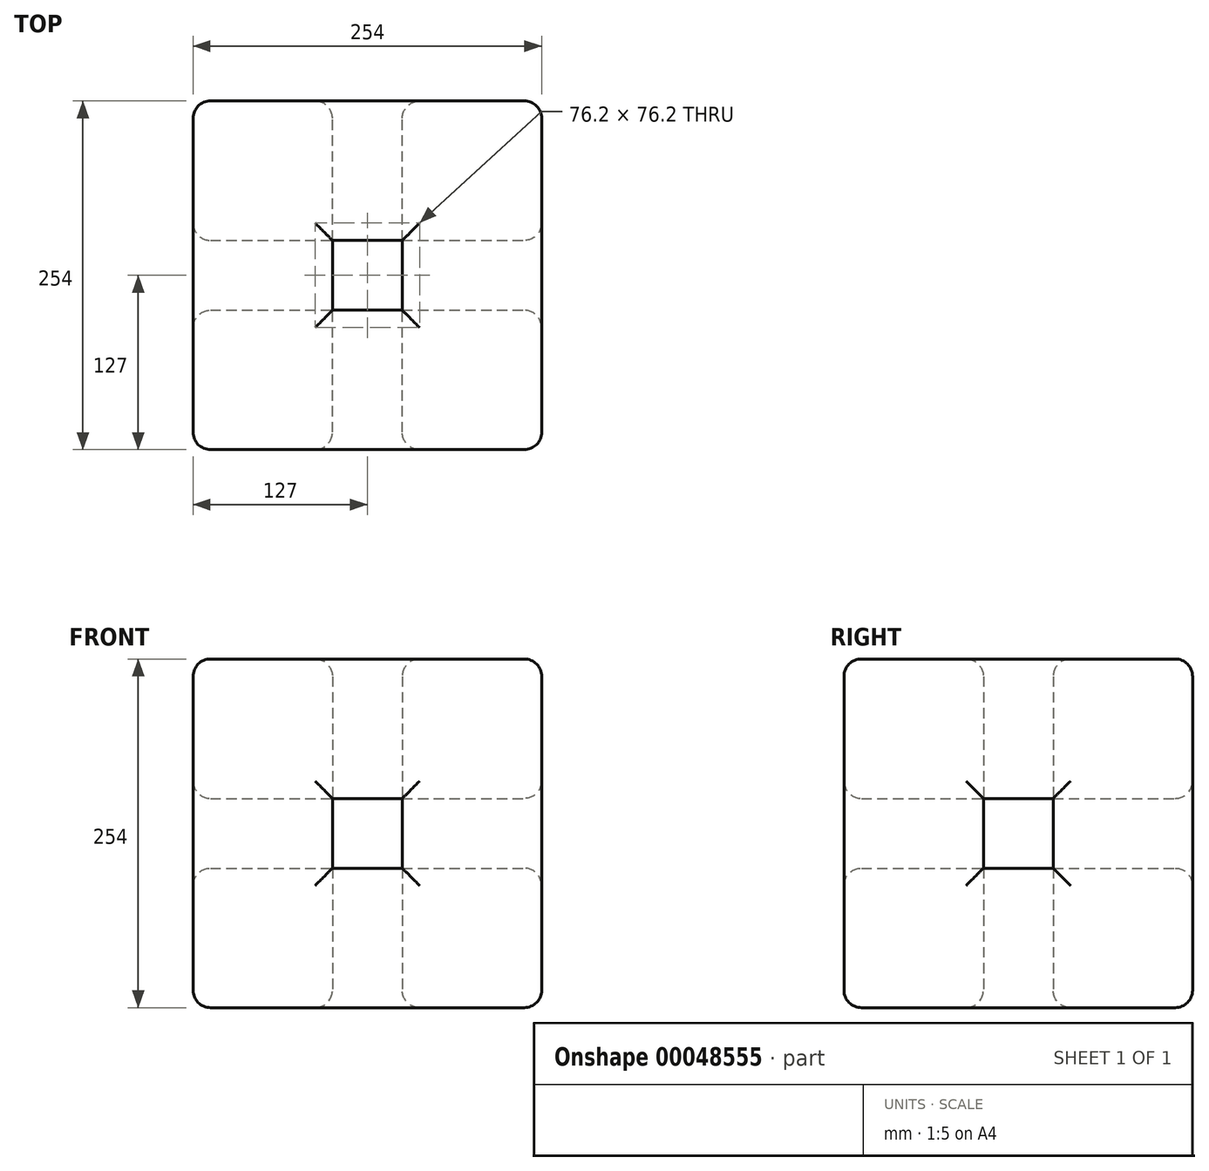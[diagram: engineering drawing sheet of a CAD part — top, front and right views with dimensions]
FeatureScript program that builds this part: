
annotation { "Feature Type Name" : "Feature", "Feature Type Description" : "" }
export const myFeature = defineFeature(function(context is Context, id is Id, definition is map)
    precondition{}
    {
        {
            var Q0;
            Q0=qCreatedBy(makeId("Front.planeOp"),FACE);
            var sketch = newSketch(context, id + "F0", { "sketchPlane" : qUnion([Q0])});
            skLineSegment(sketch, "E0.rect.bottom", {"start": v(127, 127) * mm, "end": v(-127, 127) * mm});
            skLineSegment(sketch, "E0.rect.top", {"start": v(127, -127) * mm, "end": v(-127, -127) * mm});
            skLineSegment(sketch, "E0.rect.left", {"start": v(127, 127) * mm, "end": v(127, -127) * mm});
            skLineSegment(sketch, "E0.rect.right", {"start": v(-127, 127) * mm, "end": v(-127, -127) * mm});
            skPoint(sketch, "E0.rect.middle", {"position": v(0, 0) * mm});
            skSolve(sketch);
        }
        {
            var Q0;
            Q0 = qSketchRegion(id + "F0", true);
            extrude(context, id + "F6", {"entities" : qUnion([Q0]), "endBound" : BoundingType.SYMMETRIC, "depth" : 254 * mm});
        }
        {
            var Q0;
            Q0=makeQuery(id+"F6.opExtrude","SWEPT_FACE",FACE,{"disambiguationData":[OSD([sQuery(id+"F0.wireOp",EDGE,"E0.rect.top")])]});
            var sketch = newSketch(context, id + "F7", { "sketchPlane" : qUnion([Q0])});
            skLineSegment(sketch, "E1.rect.bottom", {"start": v(25.4, 25.4) * mm, "end": v(-25.4, 25.4) * mm});
            skLineSegment(sketch, "E1.rect.top", {"start": v(25.4, -25.4) * mm, "end": v(-25.4, -25.4) * mm});
            skLineSegment(sketch, "E1.rect.left", {"start": v(25.4, 25.4) * mm, "end": v(25.4, -25.4) * mm});
            skLineSegment(sketch, "E1.rect.right", {"start": v(-25.4, 25.4) * mm, "end": v(-25.4, -25.4) * mm});
            skPoint(sketch, "E1.rect.middle", {"position": v(0, 0) * mm});
            skSolve(sketch);
        }
        {
            var Q0;
            Q0 = qSketchRegion(id + "F7", true);
            extrude(context, id + "F1", {"entities" : qUnion([Q0]), "operationType" : NewBodyOperationType.REMOVE, "endBound" : BoundingType.THROUGH_ALL, "oppositeDirection" : true, "depth" : 25.4 * mm});
        }
        {
            var Q0;
            Q0=makeQuery(id+"F6.opExtrude","SWEPT_FACE",FACE,{"disambiguationData":[OSD([sQuery(id+"F0.wireOp",EDGE,"E0.rect.left")])]});
            var sketch = newSketch(context, id + "F2", { "sketchPlane" : qUnion([Q0])});
            skLineSegment(sketch, "E2.rect.bottom", {"start": v(25.4, 25.4) * mm, "end": v(-25.4, 25.4) * mm});
            skLineSegment(sketch, "E2.rect.top", {"start": v(25.4, -25.4) * mm, "end": v(-25.4, -25.4) * mm});
            skLineSegment(sketch, "E2.rect.left", {"start": v(25.4, 25.4) * mm, "end": v(25.4, -25.4) * mm});
            skLineSegment(sketch, "E2.rect.right", {"start": v(-25.4, 25.4) * mm, "end": v(-25.4, -25.4) * mm});
            skPoint(sketch, "E2.rect.middle", {"position": v(0, 0) * mm});
            skSolve(sketch);
        }
        {
            var Q0;
            Q0 = qSketchRegion(id + "F2", true);
            extrude(context, id + "F3", {"entities" : qUnion([Q0]), "operationType" : NewBodyOperationType.REMOVE, "endBound" : BoundingType.THROUGH_ALL, "oppositeDirection" : true, "depth" : 25.4 * mm});
        }
        {
            var Q0;
            Q0=makeQuery(id+"F6.opExtrude","CAP_FACE",FACE,{"disambiguationData":[OSD([sQuery(id+"F0.wireOp",EDGE,"E0.rect.bottom"),sQuery(id+"F0.wireOp",EDGE,"E0.rect.top"),sQuery(id+"F0.wireOp",EDGE,"E0.rect.left"),sQuery(id+"F0.wireOp",EDGE,"E0.rect.right")])],"isStart":true});
            var sketch = newSketch(context, id + "F4", { "sketchPlane" : qUnion([Q0])});
            skLineSegment(sketch, "E3.rect.bottom", {"start": v(25.4, 25.4) * mm, "end": v(-25.4, 25.4) * mm});
            skLineSegment(sketch, "E3.rect.top", {"start": v(25.4, -25.4) * mm, "end": v(-25.4, -25.4) * mm});
            skLineSegment(sketch, "E3.rect.left", {"start": v(25.4, 25.4) * mm, "end": v(25.4, -25.4) * mm});
            skLineSegment(sketch, "E3.rect.right", {"start": v(-25.4, 25.4) * mm, "end": v(-25.4, -25.4) * mm});
            skPoint(sketch, "E3.rect.middle", {"position": v(0, 0) * mm});
            skSolve(sketch);
        }
        {
            var Q0;
            Q0 = qSketchRegion(id + "F4", true);
            extrude(context, id + "F8", {"entities" : qUnion([Q0]), "operationType" : NewBodyOperationType.REMOVE, "endBound" : BoundingType.THROUGH_ALL, "oppositeDirection" : true, "depth" : 25.4 * mm});
        }
        {
            var Q0;
            Q0=makeQuery(id+"F6.opExtrude","SWEPT_FACE",FACE,{"disambiguationData":[OSD([sQuery(id+"F0.wireOp",EDGE,"E0.rect.left")])]});
            var Q1;
            Q1=makeQuery(id+"F6.opExtrude","CAP_FACE",FACE,{"disambiguationData":[OSD([sQuery(id+"F0.wireOp",EDGE,"E0.rect.bottom"),sQuery(id+"F0.wireOp",EDGE,"E0.rect.top"),sQuery(id+"F0.wireOp",EDGE,"E0.rect.left"),sQuery(id+"F0.wireOp",EDGE,"E0.rect.right")])],"isStart":false});
            var Q2;
            Q2=makeQuery(id+"F6.opExtrude","SWEPT_FACE",FACE,{"disambiguationData":[OSD([sQuery(id+"F0.wireOp",EDGE,"E0.rect.right")])]});
            var Q3;
            Q3=makeQuery(id+"F6.opExtrude","CAP_FACE",FACE,{"disambiguationData":[OSD([sQuery(id+"F0.wireOp",EDGE,"E0.rect.bottom"),sQuery(id+"F0.wireOp",EDGE,"E0.rect.top"),sQuery(id+"F0.wireOp",EDGE,"E0.rect.left"),sQuery(id+"F0.wireOp",EDGE,"E0.rect.right")])],"isStart":true});
            var Q4;
            Q4=makeQuery(id+"F6.opExtrude","SWEPT_FACE",FACE,{"disambiguationData":[OSD([sQuery(id+"F0.wireOp",EDGE,"E0.rect.bottom")])]});
            var Q5;
            Q5=makeQuery(id+"F6.opExtrude","SWEPT_FACE",FACE,{"disambiguationData":[OSD([sQuery(id+"F0.wireOp",EDGE,"E0.rect.top")])]});
            fillet(context, id + "F9", {"entities" : qUnion([Q0, Q1, Q2, Q3, Q4, Q5]), "radius" : 12.7 * mm, "tangentPropagation" : true, "allowEdgeOverflow" : false});
        }
    });
